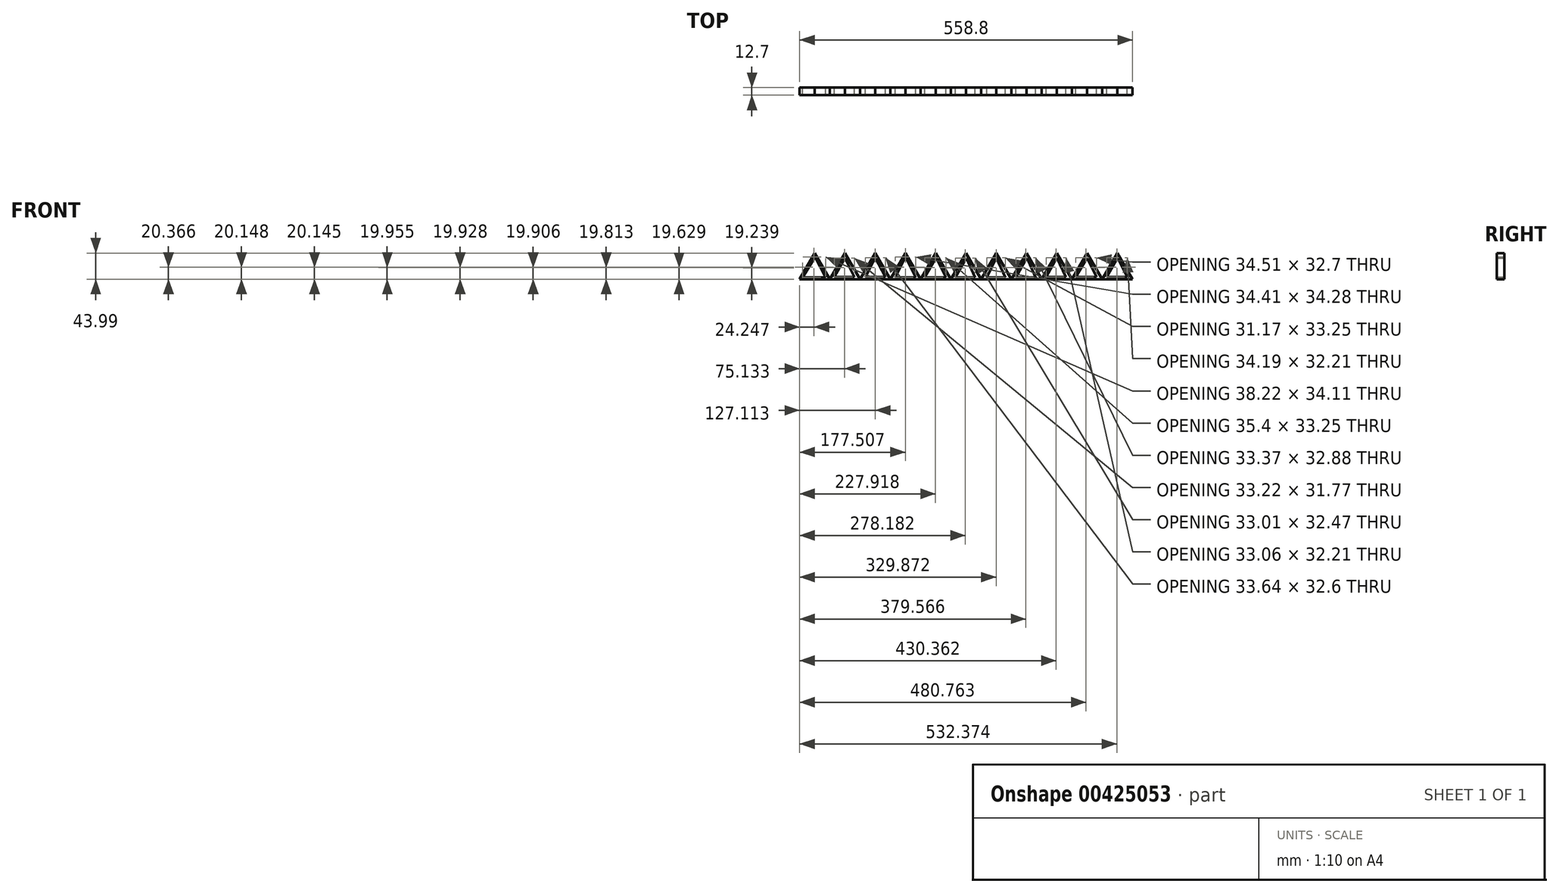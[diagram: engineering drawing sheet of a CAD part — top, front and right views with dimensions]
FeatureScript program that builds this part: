
annotation { "Feature Type Name" : "Feature", "Feature Type Description" : "" }
export const myFeature = defineFeature(function(context is Context, id is Id, definition is map)
    precondition{}
    {
        {
            var Q0;
            Q0=qCreatedBy(makeId("Front.planeOp"),FACE);
            var sketch = newSketch(context, id + "F0", { "sketchPlane" : qUnion([Q0])});
            skLineSegment(sketch, "E0", {"start": v(-267.28, -44) * mm, "end": v(-216.48, -44) * mm});
            skLineSegment(sketch, "E1", {"start": v(-216.48, -44) * mm, "end": v(-165.68, -44) * mm});
            skLineSegment(sketch, "E2", {"start": v(-165.68, -44) * mm, "end": v(-114.88, -44) * mm});
            skLineSegment(sketch, "E3", {"start": v(-114.88, -44) * mm, "end": v(-64.08, -44) * mm});
            skLineSegment(sketch, "E4", {"start": v(-64.08, -44) * mm, "end": v(-13.28, -44) * mm});
            skLineSegment(sketch, "E5", {"start": v(-13.28, -44) * mm, "end": v(37.52, -44) * mm});
            skLineSegment(sketch, "E6", {"start": v(37.52, -44) * mm, "end": v(88.32, -44) * mm});
            skLineSegment(sketch, "E7", {"start": v(88.32, -44) * mm, "end": v(139.12, -44) * mm});
            skLineSegment(sketch, "E8", {"start": v(139.12, -44) * mm, "end": v(189.92, -44) * mm});
            skLineSegment(sketch, "E9", {"start": v(189.92, -44) * mm, "end": v(240.72, -44) * mm});
            skLineSegment(sketch, "E10", {"start": v(240.72, -44) * mm, "end": v(291.52, -44) * mm});
            skLineSegment(sketch, "E11", {"start": v(-267.28, -44) * mm, "end": v(-241.88, 0) * mm});
            skLineSegment(sketch, "E12", {"start": v(-241.88, 0) * mm, "end": v(-216.48, -44) * mm});
            skLineSegment(sketch, "E13", {"start": v(-216.48, -44) * mm, "end": v(-191.08, 0) * mm});
            skLineSegment(sketch, "E14", {"start": v(-191.08, 0) * mm, "end": v(-165.68, -44) * mm});
            skLineSegment(sketch, "E15", {"start": v(-165.68, -44) * mm, "end": v(-140.28, 0) * mm});
            skLineSegment(sketch, "E16", {"start": v(-140.28, 0) * mm, "end": v(-114.88, -44) * mm});
            skLineSegment(sketch, "E17", {"start": v(-114.88, -44) * mm, "end": v(-89.48, 0) * mm});
            skLineSegment(sketch, "E18", {"start": v(-89.48, 0) * mm, "end": v(-64.08, -44) * mm});
            skLineSegment(sketch, "E19", {"start": v(-64.08, -44) * mm, "end": v(-38.68, 0) * mm});
            skLineSegment(sketch, "E20", {"start": v(-38.68, 0) * mm, "end": v(-13.28, -44) * mm});
            skLineSegment(sketch, "E21", {"start": v(-13.28, -44) * mm, "end": v(12.12, 0) * mm});
            skLineSegment(sketch, "E22", {"start": v(12.12, 0) * mm, "end": v(37.52, -44) * mm});
            skLineSegment(sketch, "E23", {"start": v(37.52, -44) * mm, "end": v(62.92, 0) * mm});
            skLineSegment(sketch, "E24", {"start": v(62.92, 0) * mm, "end": v(88.32, -44) * mm});
            skLineSegment(sketch, "E25", {"start": v(88.32, -44) * mm, "end": v(113.72, 0) * mm});
            skLineSegment(sketch, "E26", {"start": v(113.72, 0) * mm, "end": v(139.12, -44) * mm});
            skLineSegment(sketch, "E27", {"start": v(189.92, -44) * mm, "end": v(164.52, 0) * mm});
            skLineSegment(sketch, "E28", {"start": v(164.52, 0) * mm, "end": v(139.12, -44) * mm});
            skLineSegment(sketch, "E29", {"start": v(189.92, -44) * mm, "end": v(215.32, 0) * mm});
            skLineSegment(sketch, "E30", {"start": v(215.32, 0) * mm, "end": v(240.72, -44) * mm});
            skLineSegment(sketch, "E31", {"start": v(240.72, -44) * mm, "end": v(266.12, 0) * mm});
            skLineSegment(sketch, "E32", {"start": v(266.12, 0) * mm, "end": v(291.52, -44) * mm});
            skSolve(sketch);
        }
        {
            var Q0;
            Q0 = qSketchRegion(id + "F0", true);
            extrude(context, id + "F1", {"entities" : qUnion([Q0]), "depth" : 12.7 * mm});
        }
        {
            var Q0;
            Q0=qCreatedBy(makeId("Front.planeOp"),FACE);
            var sketch = newSketch(context, id + "F2", { "sketchPlane" : qUnion([Q0])});
            skLineSegment(sketch, "E33", {"start": v(-241.7, -6.57) * mm, "end": v(-262.14, -40.68) * mm});
            skLineSegment(sketch, "E34", {"start": v(-223.92, -40.68) * mm, "end": v(-241.7, -6.57) * mm});
            skLineSegment(sketch, "E35", {"start": v(-262.14, -40.68) * mm, "end": v(-223.92, -40.68) * mm});
            skSolve(sketch);
        }
        {
            var Q0;
            Q0 = qSketchRegion(id + "F2", true);
            extrude(context, id + "F3", {"entities" : qUnion([Q0]), "operationType" : NewBodyOperationType.REMOVE, "oppositeDirection" : true, "depth" : -12.7 * mm});
        }
        {
            var Q0;
            Q0=qCreatedBy(makeId("Front.planeOp"),FACE);
            var sketch = newSketch(context, id + "F4", { "sketchPlane" : qUnion([Q0])});
            skLineSegment(sketch, "E36", {"start": v(-191.34, -8.18) * mm, "end": v(-208.76, -39.95) * mm});
            skLineSegment(sketch, "E37", {"start": v(-208.76, -39.95) * mm, "end": v(-175.53, -39.95) * mm});
            skLineSegment(sketch, "E38", {"start": v(-175.53, -39.95) * mm, "end": v(-191.34, -8.18) * mm});
            skLineSegment(sketch, "E39", {"start": v(-140.49, -7.74) * mm, "end": v(-156.99, -40.33) * mm});
            skLineSegment(sketch, "E40", {"start": v(-156.99, -40.33) * mm, "end": v(-123.35, -40.33) * mm});
            skLineSegment(sketch, "E41", {"start": v(-123.35, -40.33) * mm, "end": v(-140.49, -7.74) * mm});
            skLineSegment(sketch, "E42", {"start": v(-89.7, -6.7) * mm, "end": v(-106.98, -40.99) * mm});
            skLineSegment(sketch, "E43", {"start": v(-106.98, -40.99) * mm, "end": v(-72.57, -40.99) * mm});
            skLineSegment(sketch, "E44", {"start": v(-72.57, -40.99) * mm, "end": v(-89.7, -6.7) * mm});
            skLineSegment(sketch, "E45", {"start": v(-38.54, -7.74) * mm, "end": v(-57.06, -40.99) * mm});
            skLineSegment(sketch, "E46", {"start": v(-57.06, -40.99) * mm, "end": v(-21.66, -40.99) * mm});
            skLineSegment(sketch, "E47", {"start": v(-21.66, -40.99) * mm, "end": v(-38.54, -7.74) * mm});
            skLineSegment(sketch, "E48", {"start": v(12.48, -8.52) * mm, "end": v(-5.6, -40.99) * mm});
            skLineSegment(sketch, "E49", {"start": v(-5.6, -40.99) * mm, "end": v(27.4, -40.99) * mm});
            skLineSegment(sketch, "E50", {"start": v(27.4, -40.99) * mm, "end": v(12.48, -8.52) * mm});
            skLineSegment(sketch, "E51", {"start": v(62.95, -7.74) * mm, "end": v(47, -40.99) * mm});
            skLineSegment(sketch, "E52", {"start": v(47, -40.99) * mm, "end": v(78.18, -40.99) * mm});
            skLineSegment(sketch, "E53", {"start": v(78.18, -40.99) * mm, "end": v(62.95, -7.74) * mm});
            skLineSegment(sketch, "E54", {"start": v(113.92, -7.74) * mm, "end": v(95.6, -40.62) * mm});
            skLineSegment(sketch, "E55", {"start": v(95.6, -40.62) * mm, "end": v(128.97, -40.62) * mm});
            skLineSegment(sketch, "E56", {"start": v(128.97, -40.62) * mm, "end": v(113.92, -7.74) * mm});
            skLineSegment(sketch, "E57", {"start": v(164.44, -7.74) * mm, "end": v(146.55, -39.95) * mm});
            skLineSegment(sketch, "E58", {"start": v(146.55, -39.95) * mm, "end": v(179.61, -39.95) * mm});
            skLineSegment(sketch, "E59", {"start": v(179.61, -39.95) * mm, "end": v(164.44, -7.74) * mm});
            skLineSegment(sketch, "E60", {"start": v(215.2, -7.74) * mm, "end": v(196.23, -40.43) * mm});
            skLineSegment(sketch, "E61", {"start": v(196.23, -40.43) * mm, "end": v(230.74, -40.43) * mm});
            skLineSegment(sketch, "E62", {"start": v(230.74, -40.43) * mm, "end": v(215.2, -7.74) * mm});
            skLineSegment(sketch, "E63", {"start": v(266.49, -7.74) * mm, "end": v(248, -39.95) * mm});
            skLineSegment(sketch, "E64", {"start": v(248, -39.95) * mm, "end": v(282.2, -39.95) * mm});
            skLineSegment(sketch, "E65", {"start": v(282.2, -39.95) * mm, "end": v(266.49, -7.74) * mm});
            skSolve(sketch);
        }
        {
            var Q0;
            Q0=makeQuery(id+"F4.imprint","IMPRINT",FACE,{"disambiguationData":[TD([[makeQuery(id+"F4.imprint","IMPRINT",EDGE,{"derivedFrom":sQuery(id+"F4.wireOp",EDGE,"E36")}),1.0]])]});
            var Q1;
            Q1=makeQuery(id+"F4.imprint","IMPRINT",FACE,{"disambiguationData":[TD([[makeQuery(id+"F4.imprint","IMPRINT",EDGE,{"derivedFrom":sQuery(id+"F4.wireOp",EDGE,"E39")}),1.0]])]});
            var Q2;
            Q2=makeQuery(id+"F4.imprint","IMPRINT",FACE,{"disambiguationData":[TD([[makeQuery(id+"F4.imprint","IMPRINT",EDGE,{"derivedFrom":sQuery(id+"F4.wireOp",EDGE,"E42")}),1.0]])]});
            var Q3;
            Q3=makeQuery(id+"F4.imprint","IMPRINT",FACE,{"disambiguationData":[TD([[makeQuery(id+"F4.imprint","IMPRINT",EDGE,{"derivedFrom":sQuery(id+"F4.wireOp",EDGE,"E45")}),1.0]])]});
            var Q4;
            Q4=makeQuery(id+"F4.imprint","IMPRINT",FACE,{"disambiguationData":[TD([[makeQuery(id+"F4.imprint","IMPRINT",EDGE,{"derivedFrom":sQuery(id+"F4.wireOp",EDGE,"E48")}),1.0]])]});
            var Q5;
            Q5=makeQuery(id+"F4.imprint","IMPRINT",FACE,{"disambiguationData":[TD([[makeQuery(id+"F4.imprint","IMPRINT",EDGE,{"derivedFrom":sQuery(id+"F4.wireOp",EDGE,"E51")}),1.0]])]});
            var Q6;
            Q6=makeQuery(id+"F4.imprint","IMPRINT",FACE,{"disambiguationData":[TD([[makeQuery(id+"F4.imprint","IMPRINT",EDGE,{"derivedFrom":sQuery(id+"F4.wireOp",EDGE,"E54")}),1.0]])]});
            var Q7;
            Q7=makeQuery(id+"F4.imprint","IMPRINT",FACE,{"disambiguationData":[TD([[makeQuery(id+"F4.imprint","IMPRINT",EDGE,{"derivedFrom":sQuery(id+"F4.wireOp",EDGE,"E57")}),1.0]])]});
            var Q8;
            Q8=makeQuery(id+"F4.imprint","IMPRINT",FACE,{"disambiguationData":[TD([[makeQuery(id+"F4.imprint","IMPRINT",EDGE,{"derivedFrom":sQuery(id+"F4.wireOp",EDGE,"E60")}),1.0]])]});
            var Q9;
            Q9=makeQuery(id+"F4.imprint","IMPRINT",FACE,{"disambiguationData":[TD([[makeQuery(id+"F4.imprint","IMPRINT",EDGE,{"derivedFrom":sQuery(id+"F4.wireOp",EDGE,"E63")}),1.0]])]});
            extrude(context, id + "F5", {"entities" : qUnion([Q0, Q1, Q2, Q3, Q4, Q5, Q6, Q7, Q8, Q9]), "operationType" : NewBodyOperationType.REMOVE, "depth" : 12.7 * mm});
        }
    });
